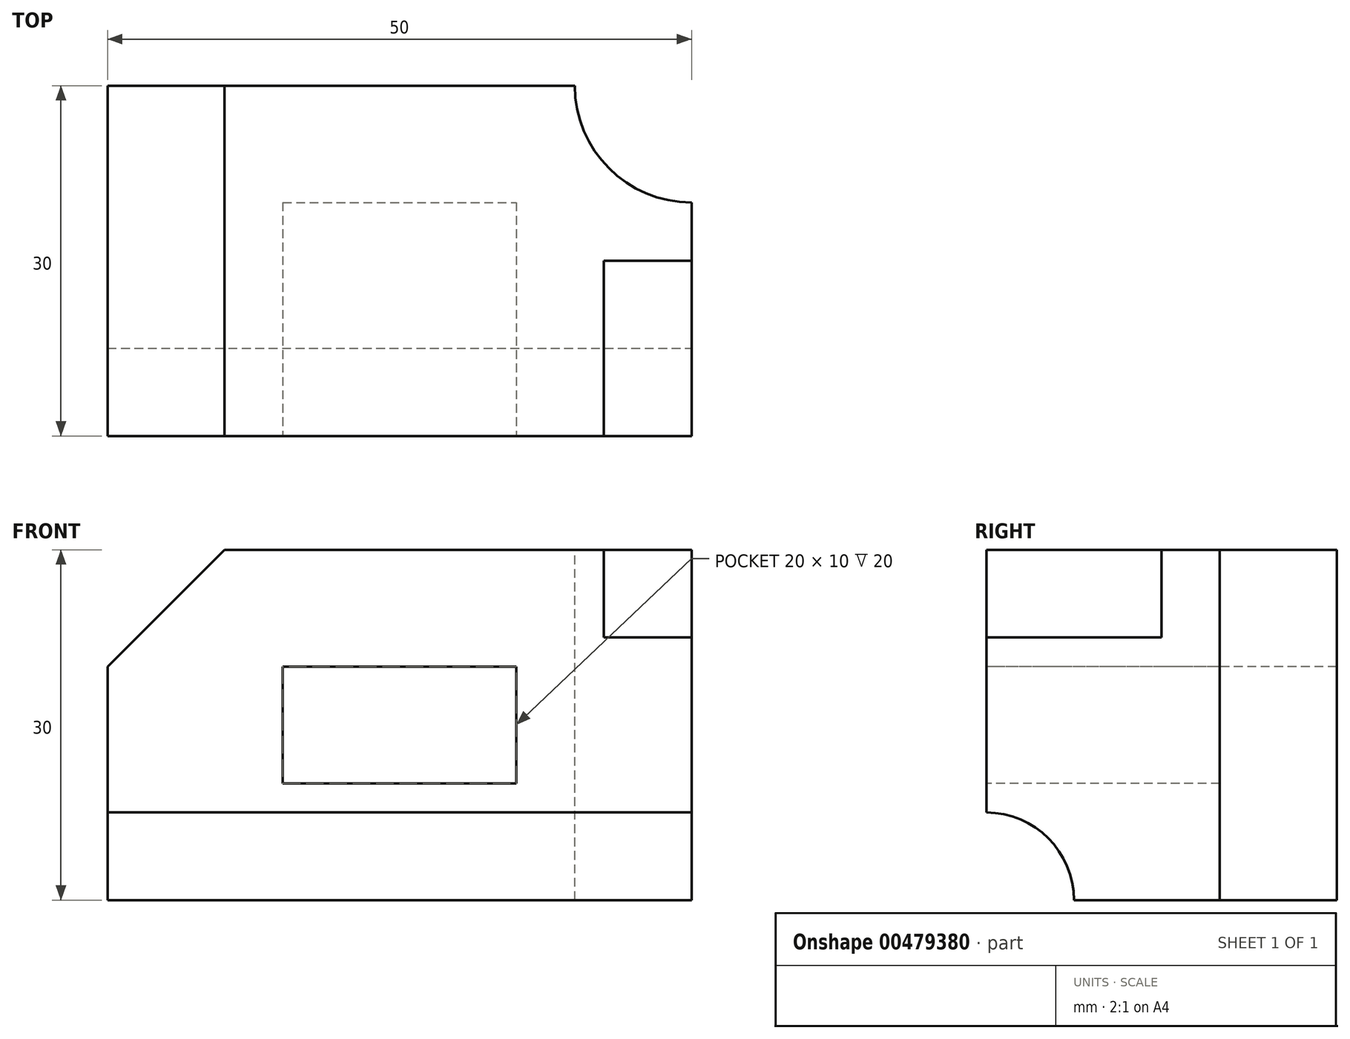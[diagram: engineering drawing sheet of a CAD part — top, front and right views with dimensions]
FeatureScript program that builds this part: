
annotation { "Feature Type Name" : "Feature", "Feature Type Description" : "" }
export const myFeature = defineFeature(function(context is Context, id is Id, definition is map)
    precondition{}
    {
        {
            var Q0;
            Q0=qCreatedBy(makeId("Top.planeOp"),FACE);
            var sketch = newSketch(context, id + "F0", { "sketchPlane" : qUnion([Q0])});
            skLineSegment(sketch, "E0.bottom", {"start": v(0, 0) * mm, "end": v(50, 0) * mm});
            skLineSegment(sketch, "E0.top", {"start": v(0, 30) * mm, "end": v(50, 30) * mm});
            skLineSegment(sketch, "E0.left", {"start": v(0, 0) * mm, "end": v(0, 30) * mm});
            skLineSegment(sketch, "E0.right", {"start": v(50, 0) * mm, "end": v(50, 30) * mm});
            skSolve(sketch);
        }
        {
            var Q0;
            Q0 = qSketchRegion(id + "F0", true);
            extrude(context, id + "F1", {"entities" : qUnion([Q0]), "depth" : 30 * mm});
        }
        {
            var Q0;
            Q0=makeQuery(id+"F1.opExtrude","SWEPT_FACE",FACE,{"disambiguationData":[OSD([sQuery(id+"F0.wireOp",EDGE,"E0.bottom")])]});
            var sketch = newSketch(context, id + "F2", { "sketchPlane" : qUnion([Q0])});
            skLineSegment(sketch, "E1.bottom", {"start": v(0, 30) * mm, "end": v(10, 30) * mm});
            skLineSegment(sketch, "E1.left", {"start": v(0, 30) * mm, "end": v(0, 20) * mm});
            skLineSegment(sketch, "E2", {"start": v(10, 30) * mm, "end": v(0, 20) * mm});
            skSolve(sketch);
        }
        {
            var Q0;
            Q0=makeQuery(id+"F2.imprint","IMPRINT",FACE,{"disambiguationData":[TD([[makeQuery(id+"F2.imprint","IMPRINT",EDGE,{"derivedFrom":sQuery(id+"F2.wireOp",EDGE,"E1.bottom")}),-1.0]])]});
            extrude(context, id + "F3", {"entities" : qUnion([Q0]), "operationType" : NewBodyOperationType.REMOVE, "endBound" : BoundingType.THROUGH_ALL, "oppositeDirection" : true, "depth" : 25 * mm});
        }
        {
            var Q0;
            Q0=makeQuery(id+"F1.opExtrude","SWEPT_FACE",FACE,{"disambiguationData":[OSD([sQuery(id+"F0.wireOp",EDGE,"E0.bottom")])]});
            var sketch = newSketch(context, id + "F4", { "sketchPlane" : qUnion([Q0])});
            skLineSegment(sketch, "E3.bottom", {"start": v(15, 20) * mm, "end": v(35, 20) * mm});
            skLineSegment(sketch, "E3.top", {"start": v(15, 10) * mm, "end": v(35, 10) * mm});
            skLineSegment(sketch, "E3.left", {"start": v(15, 20) * mm, "end": v(15, 10) * mm});
            skLineSegment(sketch, "E3.right", {"start": v(35, 20) * mm, "end": v(35, 10) * mm});
            skSolve(sketch);
        }
        {
            var Q0;
            Q0 = qSketchRegion(id + "F4", true);
            extrude(context, id + "F5", {"entities" : qUnion([Q0]), "operationType" : NewBodyOperationType.REMOVE, "oppositeDirection" : true, "depth" : 20 * mm});
        }
        {
            var Q0;
            Q0=makeQuery(id+"F1.opExtrude","CAP_FACE",FACE,{"disambiguationData":[OSD([sQuery(id+"F0.wireOp",EDGE,"E0.bottom"),sQuery(id+"F0.wireOp",EDGE,"E0.top"),sQuery(id+"F0.wireOp",EDGE,"E0.left"),sQuery(id+"F0.wireOp",EDGE,"E0.right")])],"isStart":false});
            var sketch = newSketch(context, id + "F6", { "sketchPlane" : qUnion([Q0])});
            skCircle(sketch, "E4", {"center": v(50, 30) * mm, "radius": 10 * mm});
            skSolve(sketch);
        }
        {
            var Q0;
            Q0 = qSketchRegion(id + "F6", true);
            extrude(context, id + "F7", {"entities" : qUnion([Q0]), "operationType" : NewBodyOperationType.REMOVE, "endBound" : BoundingType.THROUGH_ALL, "oppositeDirection" : true, "depth" : 25 * mm});
        }
        {
            var Q0;
            Q0=makeQuery(id+"F1.opExtrude","CAP_FACE",FACE,{"disambiguationData":[OSD([sQuery(id+"F0.wireOp",EDGE,"E0.bottom"),sQuery(id+"F0.wireOp",EDGE,"E0.top"),sQuery(id+"F0.wireOp",EDGE,"E0.left"),sQuery(id+"F0.wireOp",EDGE,"E0.right")])],"isStart":false});
            var sketch = newSketch(context, id + "F8", { "sketchPlane" : qUnion([Q0])});
            skLineSegment(sketch, "E5.bottom", {"start": v(50, 0) * mm, "end": v(42.5, 0) * mm});
            skLineSegment(sketch, "E5.top", {"start": v(50, 15) * mm, "end": v(42.5, 15) * mm});
            skLineSegment(sketch, "E5.left", {"start": v(50, 0) * mm, "end": v(50, 15) * mm});
            skLineSegment(sketch, "E5.right", {"start": v(42.5, 0) * mm, "end": v(42.5, 15) * mm});
            skSolve(sketch);
        }
        {
            var Q0;
            Q0 = qSketchRegion(id + "F8", true);
            extrude(context, id + "F9", {"entities" : qUnion([Q0]), "operationType" : NewBodyOperationType.REMOVE, "oppositeDirection" : true, "depth" : 7.5 * mm});
        }
        {
            var Q0;
            Q0=makeQuery(id+"F1.opExtrude","SWEPT_FACE",FACE,{"disambiguationData":[OSD([sQuery(id+"F0.wireOp",EDGE,"E0.right")])]});
            var sketch = newSketch(context, id + "F10", { "sketchPlane" : qUnion([Q0])});
            skCircle(sketch, "E6", {"center": v(0, 0) * mm, "radius": 7.5 * mm});
            skSolve(sketch);
        }
        {
            var Q0;
            Q0 = qSketchRegion(id + "F10", true);
            extrude(context, id + "F11", {"entities" : qUnion([Q0]), "operationType" : NewBodyOperationType.REMOVE, "endBound" : BoundingType.THROUGH_ALL, "oppositeDirection" : true, "depth" : 25 * mm});
        }
    });
